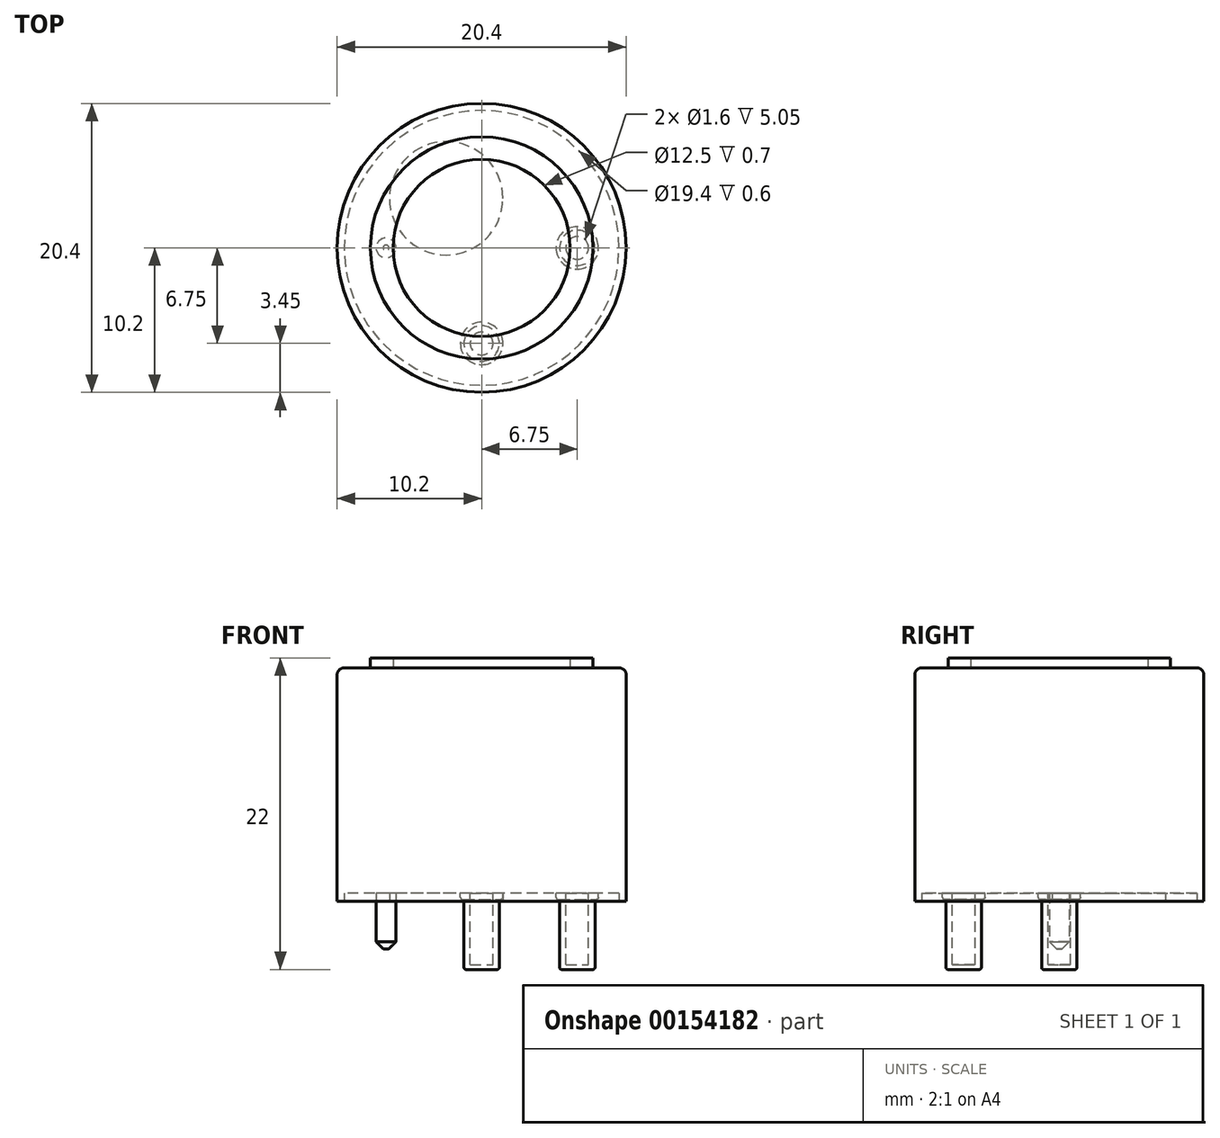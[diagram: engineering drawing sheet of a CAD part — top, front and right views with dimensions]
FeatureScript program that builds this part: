
annotation { "Feature Type Name" : "Feature", "Feature Type Description" : "" }
export const myFeature = defineFeature(function(context is Context, id is Id, definition is map)
    precondition{}
    {
        {
            var Q0;
            Q0=qCreatedBy(makeId("Top.planeOp"),FACE);
            var sketch = newSketch(context, id + "F0", { "sketchPlane" : qUnion([Q0])});
            skCircle(sketch, "E0", {"center": v(0, 0) * mm, "radius": 10.2 * mm});
            skCircle(sketch, "E1", {"center": v(0, 0) * mm, "radius": 7.85 * mm});
            skCircle(sketch, "E2", {"center": v(0, 0) * mm, "radius": 6.25 * mm});
            skCircle(sketch, "E3", {"center": v(0, 0) * mm, "radius": 5 * mm});
            skSolve(sketch);
        }
        {
            var Q0;
            Q0=makeQuery(id+"F0.imprint","IMPRINT",FACE,{"disambiguationData":[TD([[makeQuery(id+"F0.imprint","IMPRINT",EDGE,{"derivedFrom":sQuery(id+"F0.wireOp",EDGE,"E0")}),1.0]])]});
            var Q1;
            Q1=makeQuery(id+"F0.imprint","IMPRINT",FACE,{"disambiguationData":[TD([[makeQuery(id+"F0.imprint","IMPRINT",EDGE,{"derivedFrom":sQuery(id+"F0.wireOp",EDGE,"E3")}),1.0]])]});
            var Q2;
            Q2=makeQuery(id+"F0.imprint","IMPRINT",FACE,{"disambiguationData":[TD([[makeQuery(id+"F0.imprint","IMPRINT",EDGE,{"derivedFrom":sQuery(id+"F0.wireOp",EDGE,"E2")}),1.0]])]});
            var Q3;
            Q3=makeQuery(id+"F0.imprint","IMPRINT",FACE,{"disambiguationData":[TD([[makeQuery(id+"F0.imprint","IMPRINT",EDGE,{"derivedFrom":sQuery(id+"F0.wireOp",EDGE,"E1")}),1.0]])]});
            var Q4;
            Q4=sQuery(id+"F0.wireOp",EDGE,"E0");
            extrude(context, id + "F1", {"entities" : qUnion([Q0, Q1, Q2, Q3]), "surfaceEntities" : qUnion([Q4]), "depth" : 16.5 * mm});
        }
        {
            var Q0;
            Q0=makeQuery(id+"F0.imprint","IMPRINT",FACE,{"disambiguationData":[TD([[makeQuery(id+"F0.imprint","IMPRINT",EDGE,{"derivedFrom":sQuery(id+"F0.wireOp",EDGE,"E1")}),1.0]])]});
            extrude(context, id + "F2", {"entities" : qUnion([Q0]), "operationType" : NewBodyOperationType.ADD, "depth" : 17.2 * mm});
        }
        {
            var Q0;
            Q0=makeQuery(id+"F1.opExtrude","CAP_EDGE",EDGE,{"disambiguationData":[OSD([sQuery(id+"F0.wireOp",EDGE,"E0")])],"isStart":false});
            fillet(context, id + "F3", {"entities" : qUnion([Q0]), "radius" : 0.5 * mm, "tangentPropagation" : true, "allowEdgeOverflow" : false});
        }
        {
            var Q0;
            Q0=qCreatedBy(makeId("Top.planeOp"),FACE);
            var sketch = newSketch(context, id + "F4", { "sketchPlane" : qUnion([Q0])});
            skCircle(sketch, "E4", {"center": v(-6.75, 0) * mm, "radius": 0.7 * mm});
            skCircle(sketch, "E5", {"center": v(0, -6.75) * mm, "radius": 0.75 * mm});
            skCircle(sketch, "E6", {"center": v(6.75, 0) * mm, "radius": 0.75 * mm});
            skCircle(sketch, "E7", {"center": v(0, 0) * mm, "radius": 6.75 * mm, "construction": true});
            skCircle(sketch, "E8", {"center": v(-2.5, 3.5) * mm, "radius": 4 * mm});
            skCircle(sketch, "E9.0", {"center": v(0, 0) * mm, "radius": 10.2 * mm});
            skCircle(sketch, "E10", {"center": v(0, 0) * mm, "radius": 9.7 * mm});
            skSolve(sketch);
        }
        {
            var Q0;
            Q0=makeQuery(id+"F4.imprint","IMPRINT",FACE,{"disambiguationData":[TD([[makeQuery(id+"F4.imprint","IMPRINT",EDGE,{"derivedFrom":sQuery(id+"F4.wireOp",EDGE,"E4")}),-1.0]])]});
            extrude(context, id + "F5", {"entities" : qUnion([Q0]), "operationType" : NewBodyOperationType.REMOVE, "depth" : 0.6 * mm});
        }
        {
            var Q0;
            Q0=makeQuery(id+"F5.boolean.opBoolean","SPLIT",FACE,{"disambiguationData":[TD([makeQuery(id+"F5.opExtrude","SWEPT_FACE",FACE,{"disambiguationData":[OSD([sQuery(id+"F4.wireOp",EDGE,"E6")])]})])],"derivedFrom":makeQuery(id+"F1.opExtrude","CAP_FACE",FACE,{"disambiguationData":[OSD([sQuery(id+"F0.wireOp",EDGE,"E0")])],"isStart":true})});
            var Q1;
            Q1=makeQuery(id+"F5.boolean.opBoolean","SPLIT",FACE,{"disambiguationData":[TD([makeQuery(id+"F5.opExtrude","SWEPT_FACE",FACE,{"disambiguationData":[OSD([sQuery(id+"F4.wireOp",EDGE,"E5")])]})])],"derivedFrom":makeQuery(id+"F1.opExtrude","CAP_FACE",FACE,{"disambiguationData":[OSD([sQuery(id+"F0.wireOp",EDGE,"E0")])],"isStart":true})});
            extrude(context, id + "F6", {"entities" : qUnion([Q0, Q1]), "operationType" : NewBodyOperationType.ADD, "depth" : 4.35 * mm});
        }
        {
            var Q0;
            Q0=makeQuery(id+"F5.boolean.opBoolean","SPLIT",FACE,{"disambiguationData":[TD([makeQuery(id+"F5.opExtrude","SWEPT_FACE",FACE,{"disambiguationData":[OSD([sQuery(id+"F4.wireOp",EDGE,"E4")])]})])],"derivedFrom":makeQuery(id+"F1.opExtrude","CAP_FACE",FACE,{"disambiguationData":[OSD([sQuery(id+"F0.wireOp",EDGE,"E0")])],"isStart":true})});
            extrude(context, id + "F7", {"entities" : qUnion([Q0]), "operationType" : NewBodyOperationType.ADD, "depth" : 3.35 * mm});
        }
        {
            var Q0;
            Q0=makeQuery(id+"F6.opExtrude","CAP_EDGE",EDGE,{"disambiguationData":[OSD([sQuery(id+"F4.wireOp",EDGE,"E6")])],"isStart":false});
            var Q1;
            Q1=makeQuery(id+"F6.opExtrude","CAP_EDGE",EDGE,{"disambiguationData":[OSD([sQuery(id+"F4.wireOp",EDGE,"E5")])],"isStart":false});
            chamfer(context, id + "F8", {"entities" : qUnion([Q0, Q1]), "chamferType" : ChamferType.TWO_OFFSETS, "width1" : 1 * mm, "oppositeDirection" : false, "width2" : 0.4 * mm, "tangentPropagation" : true});
        }
        {
            var Q0;
            Q0=makeQuery(id+"F7.opExtrude","CAP_EDGE",EDGE,{"disambiguationData":[OSD([sQuery(id+"F4.wireOp",EDGE,"E4")])],"isStart":false});
            chamfer(context, id + "F9", {"entities" : qUnion([Q0]), "width" : 0.5 * mm, "tangentPropagation" : true});
        }
        {
            var Q0;
            Q0=makeQuery(id+"F5.boolean.opBoolean","COPY",FACE,{"derivedFrom":makeQuery(id+"F5.opExtrude","CAP_FACE",FACE,{"disambiguationData":[OSD([sQuery(id+"F4.wireOp",EDGE,"E4"),sQuery(id+"F4.wireOp",EDGE,"E5"),sQuery(id+"F4.wireOp",EDGE,"E6"),sQuery(id+"F4.wireOp",EDGE,"E8"),sQuery(id+"F4.wireOp",EDGE,"E10")])],"isStart":false})});
            var sketch = newSketch(context, id + "F10", { "sketchPlane" : qUnion([Q0])});
            skCircle(sketch, "E11", {"center": v(6.75, 0) * mm, "radius": 0.8 * mm});
            skCircle(sketch, "E12", {"center": v(0, 6.75) * mm, "radius": 0.8 * mm});
            skCircle(sketch, "E13", {"center": v(6.75, 0) * mm, "radius": 1.25 * mm});
            skCircle(sketch, "E14", {"center": v(0, 6.75) * mm, "radius": 1.25 * mm});
            skCircle(sketch, "E15", {"center": v(0, 6.75) * mm, "radius": 1.5 * mm});
            skCircle(sketch, "E16", {"center": v(6.75, 0) * mm, "radius": 1.5 * mm});
            skSolve(sketch);
        }
        {
            var Q0;
            Q0=makeQuery(id+"F10.imprint","IMPRINT",FACE,{"disambiguationData":[TD([[makeQuery(id+"F10.imprint","IMPRINT",EDGE,{"derivedFrom":sQuery(id+"F10.wireOp",EDGE,"E11")}),-1.0]])]});
            var Q1;
            Q1=makeQuery(id+"F10.imprint","IMPRINT",FACE,{"disambiguationData":[TD([[makeQuery(id+"F10.imprint","IMPRINT",EDGE,{"derivedFrom":makeQuery(id+"F5.boolean.opBoolean","COPY",EDGE,{"derivedFrom":makeQuery(id+"F5.opExtrude","CAP_EDGE",EDGE,{"disambiguationData":[OSD([sQuery(id+"F4.wireOp",EDGE,"E6")])],"isStart":false})})}),-1.0]])]});
            var Q2;
            Q2=makeQuery(id+"F10.imprint","IMPRINT",FACE,{"disambiguationData":[TD([[makeQuery(id+"F10.imprint","IMPRINT",EDGE,{"derivedFrom":sQuery(id+"F10.wireOp",EDGE,"E12")}),-1.0]])]});
            var Q3;
            Q3=makeQuery(id+"F10.imprint","IMPRINT",FACE,{"disambiguationData":[TD([[makeQuery(id+"F10.imprint","IMPRINT",EDGE,{"derivedFrom":makeQuery(id+"F5.boolean.opBoolean","COPY",EDGE,{"derivedFrom":makeQuery(id+"F5.opExtrude","CAP_EDGE",EDGE,{"disambiguationData":[OSD([sQuery(id+"F4.wireOp",EDGE,"E5")])],"isStart":false})})}),-1.0]])]});
            var Q4;
            Q4=makeQuery(id+"F10.imprint","IMPRINT",FACE,{"disambiguationData":[TD([[makeQuery(id+"F10.imprint","IMPRINT",EDGE,{"derivedFrom":sQuery(id+"F10.wireOp",EDGE,"E11")}),1.0]])]});
            var Q5;
            Q5=makeQuery(id+"F10.imprint","IMPRINT",FACE,{"disambiguationData":[TD([[makeQuery(id+"F10.imprint","IMPRINT",EDGE,{"derivedFrom":sQuery(id+"F10.wireOp",EDGE,"E12")}),1.0]])]});
            extrude(context, id + "F11", {"entities" : qUnion([Q0, Q1, Q2, Q3, Q4, Q5]), "depth" : 5.4 * mm});
        }
        {
            var Q0;
            Q0=makeQuery(id+"F10.imprint","IMPRINT",FACE,{"disambiguationData":[TD([[makeQuery(id+"F10.imprint","IMPRINT",EDGE,{"derivedFrom":sQuery(id+"F10.wireOp",EDGE,"E13")}),-1.0]])]});
            var Q1;
            Q1=makeQuery(id+"F10.imprint","IMPRINT",FACE,{"disambiguationData":[TD([[makeQuery(id+"F10.imprint","IMPRINT",EDGE,{"derivedFrom":sQuery(id+"F10.wireOp",EDGE,"E14")}),-1.0]])]});
            extrude(context, id + "F12", {"entities" : qUnion([Q0, Q1]), "operationType" : NewBodyOperationType.ADD, "depth" : 0.45 * mm});
        }
        {
            var Q0;
            Q0=makeQuery(id+"F10.imprint","IMPRINT",FACE,{"disambiguationData":[TD([[makeQuery(id+"F10.imprint","IMPRINT",EDGE,{"derivedFrom":makeQuery(id+"F5.boolean.opBoolean","COPY",EDGE,{"derivedFrom":makeQuery(id+"F5.opExtrude","CAP_EDGE",EDGE,{"disambiguationData":[OSD([sQuery(id+"F4.wireOp",EDGE,"E6")])],"isStart":false})})}),-1.0]])]});
            var Q1;
            Q1=makeQuery(id+"F10.imprint","IMPRINT",FACE,{"disambiguationData":[TD([[makeQuery(id+"F10.imprint","IMPRINT",EDGE,{"derivedFrom":sQuery(id+"F10.wireOp",EDGE,"E11")}),1.0]])]});
            var Q2;
            Q2=makeQuery(id+"F10.imprint","IMPRINT",FACE,{"disambiguationData":[TD([[makeQuery(id+"F10.imprint","IMPRINT",EDGE,{"derivedFrom":makeQuery(id+"F5.boolean.opBoolean","COPY",EDGE,{"derivedFrom":makeQuery(id+"F5.opExtrude","CAP_EDGE",EDGE,{"disambiguationData":[OSD([sQuery(id+"F4.wireOp",EDGE,"E5")])],"isStart":false})})}),-1.0]])]});
            var Q3;
            Q3=makeQuery(id+"F10.imprint","IMPRINT",FACE,{"disambiguationData":[TD([[makeQuery(id+"F10.imprint","IMPRINT",EDGE,{"derivedFrom":sQuery(id+"F10.wireOp",EDGE,"E12")}),1.0]])]});
            extrude(context, id + "F13", {"entities" : qUnion([Q0, Q1, Q2, Q3]), "operationType" : NewBodyOperationType.REMOVE, "depth" : 5.05 * mm});
        }
        {
            var Q0;
            Q0=makeQuery(id+"F12.opExtrude","CAP_EDGE",EDGE,{"disambiguationData":[OSD([sQuery(id+"F10.wireOp",EDGE,"E15")])],"isStart":true});
            var Q1;
            Q1=makeQuery(id+"F12.opExtrude","CAP_EDGE",EDGE,{"disambiguationData":[OSD([sQuery(id+"F10.wireOp",EDGE,"E15")])],"isStart":false});
            var Q2;
            Q2=makeQuery(id+"F11.opExtrude","CAP_EDGE",EDGE,{"disambiguationData":[OSD([sQuery(id+"F10.wireOp",EDGE,"E14")])],"isStart":false});
            var Q3;
            Q3=makeQuery(id+"F11.opExtrude","CAP_EDGE",EDGE,{"disambiguationData":[OSD([sQuery(id+"F10.wireOp",EDGE,"E13")])],"isStart":false});
            var Q4;
            Q4=makeQuery(id+"F12.opExtrude","CAP_EDGE",EDGE,{"disambiguationData":[OSD([sQuery(id+"F10.wireOp",EDGE,"E16")])],"isStart":false});
            var Q5;
            Q5=makeQuery(id+"F12.opExtrude","CAP_EDGE",EDGE,{"disambiguationData":[OSD([sQuery(id+"F10.wireOp",EDGE,"E16")])],"isStart":true});
            fillet(context, id + "F14", {"entities" : qUnion([Q0, Q1, Q2, Q3, Q4, Q5]), "radius" : 0.15 * mm, "tangentPropagation" : true, "allowEdgeOverflow" : false});
        }
    });
